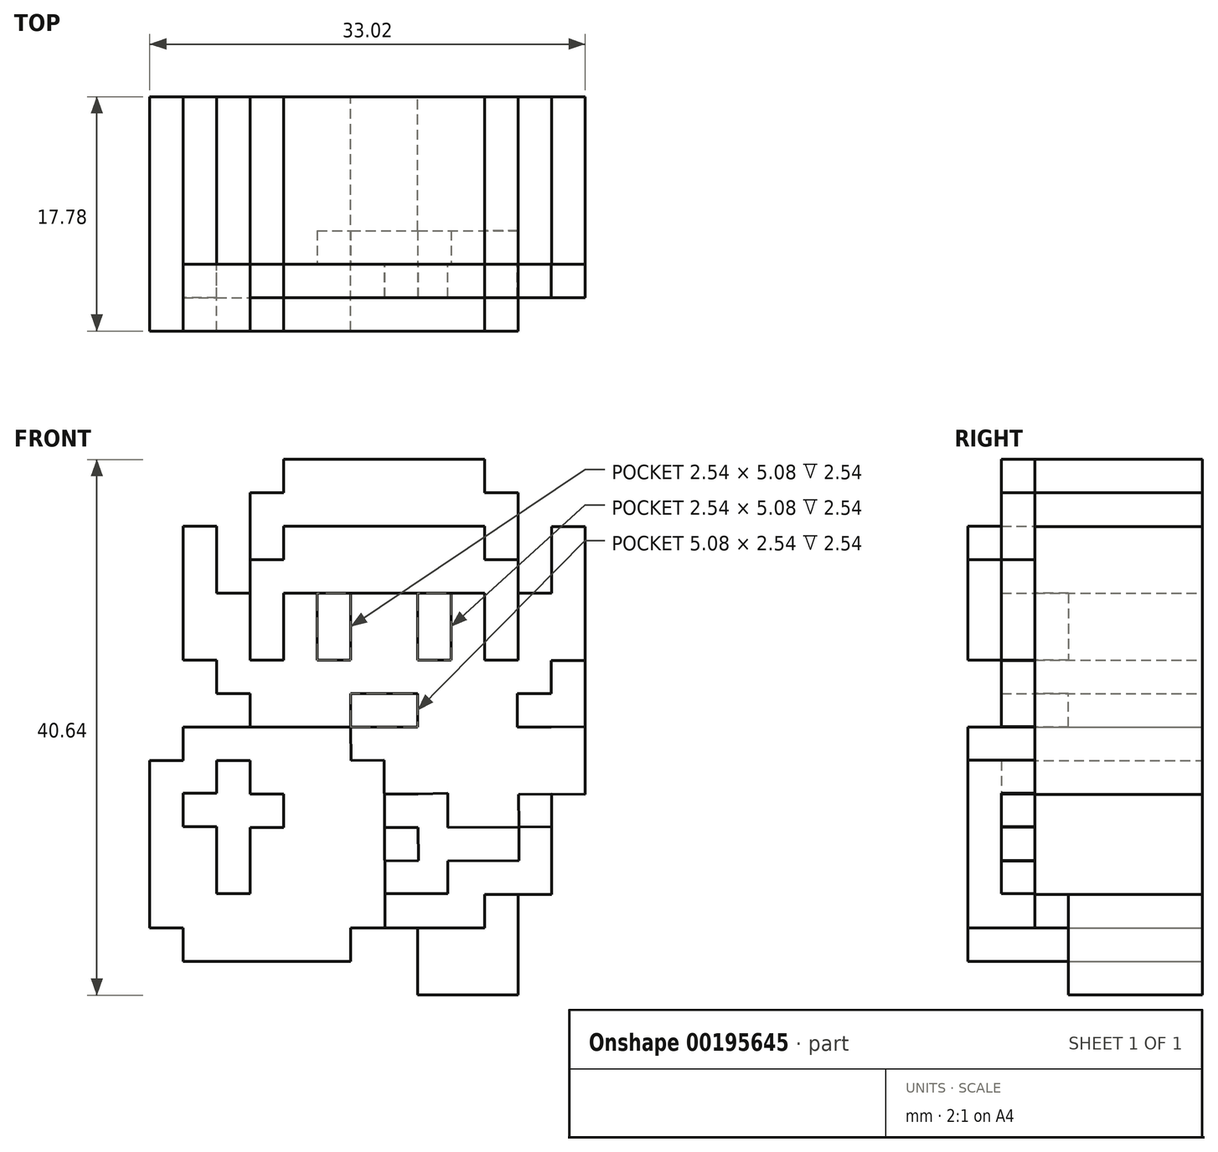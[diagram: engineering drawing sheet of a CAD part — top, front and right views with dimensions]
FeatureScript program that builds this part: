
annotation { "Feature Type Name" : "Feature", "Feature Type Description" : "" }
export const myFeature = defineFeature(function(context is Context, id is Id, definition is map)
    precondition{}
    {
        {
            var Q0;
            Q0=qCreatedBy(makeId("Front.planeOp"),FACE);
            var sketch = newSketch(context, id + "F0", { "sketchPlane" : qUnion([Q0])});
            skLineSegment(sketch, "E0", {"start": v(-12.95, 10.7) * mm, "end": v(2.29, 10.7) * mm});
            skLineSegment(sketch, "E1", {"start": v(-12.95, 10.7) * mm, "end": v(-12.95, 8.15) * mm});
            skLineSegment(sketch, "E2", {"start": v(-12.95, 8.15) * mm, "end": v(-15.5, 8.15) * mm});
            skLineSegment(sketch, "E3", {"start": v(2.29, 10.7) * mm, "end": v(2.29, 8.15) * mm});
            skLineSegment(sketch, "E4", {"start": v(2.29, 8.15) * mm, "end": v(4.83, 8.15) * mm});
            skLineSegment(sketch, "E5", {"start": v(-15.5, 8.15) * mm, "end": v(-15.5, 0.53) * mm});
            skLineSegment(sketch, "E6", {"start": v(4.83, 8.15) * mm, "end": v(4.83, 0.53) * mm});
            skLineSegment(sketch, "E7", {"start": v(-15.5, 0.53) * mm, "end": v(-18.03, 0.53) * mm});
            skLineSegment(sketch, "E8", {"start": v(-18.03, 0.53) * mm, "end": v(-18.03, 5.61) * mm});
            skLineSegment(sketch, "E9", {"start": v(-18.03, 5.61) * mm, "end": v(-20.57, 5.61) * mm});
            skLineSegment(sketch, "E10", {"start": v(-20.57, 5.61) * mm, "end": v(-20.57, -4.55) * mm});
            skLineSegment(sketch, "E11", {"start": v(-20.57, -4.55) * mm, "end": v(-18.03, -4.55) * mm});
            skLineSegment(sketch, "E12", {"start": v(-18.03, -4.55) * mm, "end": v(-18.03, -7.09) * mm});
            skLineSegment(sketch, "E13", {"start": v(-18.03, -7.09) * mm, "end": v(-15.5, -7.09) * mm});
            skLineSegment(sketch, "E14", {"start": v(-15.5, -7.09) * mm, "end": v(-15.5, -9.63) * mm});
            skLineSegment(sketch, "E15", {"start": v(4.83, 0.53) * mm, "end": v(7.37, 0.53) * mm});
            skLineSegment(sketch, "E16", {"start": v(7.37, 0.53) * mm, "end": v(7.37, 5.61) * mm});
            skLineSegment(sketch, "E17", {"start": v(7.37, 5.61) * mm, "end": v(9.9, 5.61) * mm});
            skLineSegment(sketch, "E18", {"start": v(9.9, 5.61) * mm, "end": v(9.9, -14.7) * mm});
            skLineSegment(sketch, "E19", {"start": v(-15.5, -9.63) * mm, "end": v(-20.57, -9.63) * mm});
            skLineSegment(sketch, "E20", {"start": v(-20.57, -9.63) * mm, "end": v(-20.57, -12.17) * mm});
            skLineSegment(sketch, "E21", {"start": v(-20.57, -12.17) * mm, "end": v(-23.11, -12.17) * mm});
            skLineSegment(sketch, "E22", {"start": v(-23.11, -12.17) * mm, "end": v(-23.11, -24.87) * mm});
            skLineSegment(sketch, "E23", {"start": v(-23.11, -24.87) * mm, "end": v(-20.57, -24.87) * mm});
            skLineSegment(sketch, "E24", {"start": v(-20.57, -24.87) * mm, "end": v(-20.57, -27.4) * mm});
            skLineSegment(sketch, "E25", {"start": v(-20.57, -27.4) * mm, "end": v(-7.87, -27.4) * mm});
            skLineSegment(sketch, "E26", {"start": v(-7.87, -27.4) * mm, "end": v(-7.87, -24.87) * mm});
            skLineSegment(sketch, "E27", {"start": v(-7.87, -24.87) * mm, "end": v(-2.8, -24.87) * mm});
            skLineSegment(sketch, "E28", {"start": v(-2.8, -24.87) * mm, "end": v(-2.8, -29.95) * mm});
            skLineSegment(sketch, "E29", {"start": v(-2.8, -29.95) * mm, "end": v(4.83, -29.95) * mm});
            skLineSegment(sketch, "E30", {"start": v(4.83, -29.95) * mm, "end": v(4.83, -22.33) * mm});
            skLineSegment(sketch, "E31", {"start": v(4.83, -22.33) * mm, "end": v(7.37, -22.33) * mm});
            skLineSegment(sketch, "E32", {"start": v(7.37, -22.33) * mm, "end": v(7.37, -14.7) * mm});
            skLineSegment(sketch, "E33", {"start": v(7.37, -14.7) * mm, "end": v(9.9, -14.7) * mm});
            skSolve(sketch);
        }
        {
            var Q0;
            Q0=makeQuery(id+"F0.imprint","IMPRINT",FACE,{"disambiguationData":[TD([[makeQuery(id+"F0.imprint","IMPRINT",EDGE,{"derivedFrom":sQuery(id+"F0.wireOp",EDGE,"E0")}),-1.0]])]});
            extrude(context, id + "F1", {"entities" : qUnion([Q0]), "depth" : 12.7 * mm});
        }
        {
            var Q0;
            Q0=makeQuery(id+"F1.opExtrude","CAP_FACE",FACE,{"disambiguationData":[OSD([sQuery(id+"F0.wireOp",EDGE,"E0"),sQuery(id+"F0.wireOp",EDGE,"E1"),sQuery(id+"F0.wireOp",EDGE,"E2"),sQuery(id+"F0.wireOp",EDGE,"E3"),sQuery(id+"F0.wireOp",EDGE,"E4"),sQuery(id+"F0.wireOp",EDGE,"E5"),sQuery(id+"F0.wireOp",EDGE,"E6"),sQuery(id+"F0.wireOp",EDGE,"E7"),sQuery(id+"F0.wireOp",EDGE,"E8"),sQuery(id+"F0.wireOp",EDGE,"E9"),sQuery(id+"F0.wireOp",EDGE,"E10"),sQuery(id+"F0.wireOp",EDGE,"E11"),sQuery(id+"F0.wireOp",EDGE,"E12"),sQuery(id+"F0.wireOp",EDGE,"E13"),sQuery(id+"F0.wireOp",EDGE,"E14"),sQuery(id+"F0.wireOp",EDGE,"E15"),sQuery(id+"F0.wireOp",EDGE,"E16"),sQuery(id+"F0.wireOp",EDGE,"E17"),sQuery(id+"F0.wireOp",EDGE,"E18"),sQuery(id+"F0.wireOp",EDGE,"E19"),sQuery(id+"F0.wireOp",EDGE,"E20"),sQuery(id+"F0.wireOp",EDGE,"E21"),sQuery(id+"F0.wireOp",EDGE,"E22"),sQuery(id+"F0.wireOp",EDGE,"E23"),sQuery(id+"F0.wireOp",EDGE,"E24"),sQuery(id+"F0.wireOp",EDGE,"E25"),sQuery(id+"F0.wireOp",EDGE,"E26"),sQuery(id+"F0.wireOp",EDGE,"E27"),sQuery(id+"F0.wireOp",EDGE,"E28"),sQuery(id+"F0.wireOp",EDGE,"E29"),sQuery(id+"F0.wireOp",EDGE,"E30"),sQuery(id+"F0.wireOp",EDGE,"E31"),sQuery(id+"F0.wireOp",EDGE,"E32"),sQuery(id+"F0.wireOp",EDGE,"E33")])],"isStart":false});
            var sketch = newSketch(context, id + "F2", { "sketchPlane" : qUnion([Q0])});
            skLineSegment(sketch, "E34", {"start": v(-15.5, 8.15) * mm, "end": v(-15.5, 3.07) * mm});
            skLineSegment(sketch, "E35", {"start": v(-15.5, 3.07) * mm, "end": v(-12.95, 3.07) * mm});
            skLineSegment(sketch, "E36", {"start": v(-12.95, 3.07) * mm, "end": v(-12.95, 5.61) * mm});
            skLineSegment(sketch, "E37", {"start": v(-12.95, 5.61) * mm, "end": v(2.3, 5.61) * mm});
            skLineSegment(sketch, "E38", {"start": v(2.3, 5.61) * mm, "end": v(2.3, 3.07) * mm});
            skLineSegment(sketch, "E39", {"start": v(2.3, 3.07) * mm, "end": v(4.83, 3.07) * mm});
            skLineSegment(sketch, "E40", {"start": v(-15.5, 0.53) * mm, "end": v(-15.5, -4.55) * mm});
            skLineSegment(sketch, "E41", {"start": v(-15.5, -4.55) * mm, "end": v(-12.95, -4.55) * mm});
            skLineSegment(sketch, "E42", {"start": v(-12.95, -4.55) * mm, "end": v(-12.95, 0.53) * mm});
            skLineSegment(sketch, "E43", {"start": v(-12.95, 0.53) * mm, "end": v(2.29, 0.53) * mm});
            skLineSegment(sketch, "E44", {"start": v(2.29, 0.53) * mm, "end": v(2.29, -4.55) * mm});
            skLineSegment(sketch, "E45", {"start": v(2.29, -4.55) * mm, "end": v(4.83, -4.55) * mm});
            skLineSegment(sketch, "E46", {"start": v(4.83, -4.55) * mm, "end": v(4.83, 0.53) * mm});
            skLineSegment(sketch, "E47", {"start": v(-12.95, 0.53) * mm, "end": v(-10.41, 0.53) * mm});
            skLineSegment(sketch, "E48", {"start": v(-10.41, 0.53) * mm, "end": v(-10.41, -4.55) * mm});
            skLineSegment(sketch, "E49", {"start": v(-10.41, -4.55) * mm, "end": v(-7.87, -4.55) * mm});
            skLineSegment(sketch, "E50", {"start": v(-7.87, -4.55) * mm, "end": v(-7.87, 0.53) * mm});
            skLineSegment(sketch, "E51", {"start": v(-7.87, 0.53) * mm, "end": v(-2.8, 0.53) * mm});
            skLineSegment(sketch, "E52", {"start": v(-2.8, 0.53) * mm, "end": v(-2.8, -4.55) * mm});
            skLineSegment(sketch, "E53", {"start": v(-2.8, -4.55) * mm, "end": v(-0.26, -4.55) * mm});
            skLineSegment(sketch, "E54", {"start": v(-0.26, -4.55) * mm, "end": v(-0.26, 0.53) * mm});
            skLineSegment(sketch, "E55", {"start": v(-7.87, -7.06) * mm, "end": v(-2.8, -7.06) * mm});
            skLineSegment(sketch, "E56", {"start": v(-2.8, -7.06) * mm, "end": v(-2.8, -9.6) * mm});
            skLineSegment(sketch, "E57", {"start": v(-2.8, -9.6) * mm, "end": v(-7.87, -9.6) * mm});
            skLineSegment(sketch, "E58", {"start": v(-7.87, -9.6) * mm, "end": v(-7.87, -7.06) * mm});
            skLineSegment(sketch, "E59", {"start": v(-15.5, -7.09) * mm, "end": v(-12.95, -7.09) * mm});
            skLineSegment(sketch, "E60", {"start": v(-12.95, -7.09) * mm, "end": v(-12.95, -9.63) * mm});
            skLineSegment(sketch, "E61", {"start": v(-12.95, -9.63) * mm, "end": v(-15.5, -9.63) * mm});
            skLineSegment(sketch, "E62", {"start": v(-12.95, -9.63) * mm, "end": v(-7.87, -9.6) * mm});
            skLineSegment(sketch, "E63", {"start": v(-7.87, -9.6) * mm, "end": v(-7.86, -12.14) * mm});
            skLineSegment(sketch, "E64", {"start": v(-7.86, -12.14) * mm, "end": v(-5.32, -12.12) * mm});
            skPoint(sketch, "E65.endSnap0", {"position": v(-5.33, -24.87) * mm});
            skLineSegment(sketch, "E66", {"start": v(-5.32, -12.12) * mm, "end": v(-5.27, -22.26) * mm});
            skLineSegment(sketch, "E67", {"start": v(-20.57, -12.17) * mm, "end": v(-18.03, -12.17) * mm});
            skLineSegment(sketch, "E68", {"start": v(-18.03, -12.17) * mm, "end": v(-18.03, -14.62) * mm});
            skLineSegment(sketch, "E69", {"start": v(-18.03, -12.17) * mm, "end": v(-15.49, -12.17) * mm});
            skLineSegment(sketch, "E70", {"start": v(-15.49, -12.17) * mm, "end": v(-15.49, -14.7) * mm});
            skLineSegment(sketch, "E71", {"start": v(-15.49, -14.7) * mm, "end": v(-12.95, -14.7) * mm});
            skLineSegment(sketch, "E72", {"start": v(-12.95, -14.7) * mm, "end": v(-12.95, -17.25) * mm});
            skLineSegment(sketch, "E73", {"start": v(-12.95, -17.25) * mm, "end": v(-15.49, -17.25) * mm});
            skLineSegment(sketch, "E74", {"start": v(-18.03, -14.62) * mm, "end": v(-20.57, -14.62) * mm});
            skLineSegment(sketch, "E75", {"start": v(-20.57, -14.62) * mm, "end": v(-20.57, -17.16) * mm});
            skLineSegment(sketch, "E76", {"start": v(-20.57, -17.16) * mm, "end": v(-18.03, -17.16) * mm});
            skLineSegment(sketch, "E77", {"start": v(-18.03, -17.16) * mm, "end": v(-18.03, -22.24) * mm});
            skLineSegment(sketch, "E78", {"start": v(-18.03, -22.24) * mm, "end": v(-15.49, -22.24) * mm});
            skLineSegment(sketch, "E79", {"start": v(-15.49, -22.24) * mm, "end": v(-15.49, -17.25) * mm});
            skLineSegment(sketch, "E80", {"start": v(-5.32, -12.12) * mm, "end": v(-5.3, -14.68) * mm});
            skLineSegment(sketch, "E81", {"start": v(-5.3, -14.68) * mm, "end": v(-2.77, -14.68) * mm});
            skLineSegment(sketch, "E82", {"start": v(-2.76, -17.22) * mm, "end": v(-5.3, -17.22) * mm});
            skLineSegment(sketch, "E83", {"start": v(-2.76, -17.22) * mm, "end": v(-2.74, -19.75) * mm});
            skLineSegment(sketch, "E84", {"start": v(-2.74, -19.75) * mm, "end": v(-5.3, -19.76) * mm});
            skLineSegment(sketch, "E85", {"start": v(-2.73, -22.24) * mm, "end": v(-5.27, -22.26) * mm});
            skLineSegment(sketch, "E86", {"start": v(-2.73, -22.24) * mm, "end": v(-0.52, -22.24) * mm});
            skLineSegment(sketch, "E87", {"start": v(-0.52, -22.24) * mm, "end": v(-0.52, -19.78) * mm});
            skLineSegment(sketch, "E88", {"start": v(-0.52, -14.62) * mm, "end": v(-2.77, -14.68) * mm});
            skLineSegment(sketch, "E89", {"start": v(-0.52, -17.22) * mm, "end": v(7.37, -17.17) * mm});
            skLineSegment(sketch, "E90", {"start": v(7.37, -14.7) * mm, "end": v(4.87, -14.72) * mm});
            skLineSegment(sketch, "E91", {"start": v(4.87, -14.72) * mm, "end": v(4.88, -17.17) * mm});
            skLineSegment(sketch, "E92", {"start": v(4.88, -17.17) * mm, "end": v(4.9, -19.75) * mm});
            skLineSegment(sketch, "E93", {"start": v(4.9, -19.75) * mm, "end": v(-0.52, -19.78) * mm});
            skLineSegment(sketch, "E94", {"start": v(7.37, -14.7) * mm, "end": v(7.34, -9.6) * mm});
            skLineSegment(sketch, "E95", {"start": v(7.34, -9.6) * mm, "end": v(9.9, -9.59) * mm});
            skLineSegment(sketch, "E96", {"start": v(9.9, -9.59) * mm, "end": v(9.9, -4.55) * mm});
            skLineSegment(sketch, "E97", {"start": v(9.9, -4.55) * mm, "end": v(7.34, -4.55) * mm});
            skLineSegment(sketch, "E98", {"start": v(7.34, -4.55) * mm, "end": v(7.34, -7.07) * mm});
            skPoint(sketch, "E98.endSnap0", {"position": v(9.9, -7.07) * mm});
            skLineSegment(sketch, "E99", {"start": v(7.34, -7.07) * mm, "end": v(4.76, -7.07) * mm});
            skLineSegment(sketch, "E100", {"start": v(4.76, -7.07) * mm, "end": v(4.76, -9.6) * mm});
            skLineSegment(sketch, "E101", {"start": v(4.76, -9.6) * mm, "end": v(7.34, -9.6) * mm});
            skLineSegment(sketch, "E102", {"start": v(-2.8, -24.87) * mm, "end": v(2.28, -24.87) * mm});
            skPoint(sketch, "E102.endSnap0", {"position": v(4.83, -26.14) * mm});
            skLineSegment(sketch, "E103", {"start": v(4.83, -24.87) * mm, "end": v(4.83, -22.33) * mm});
            skLineSegment(sketch, "E104", {"start": v(4.83, -22.33) * mm, "end": v(2.28, -22.33) * mm});
            skLineSegment(sketch, "E105", {"start": v(2.28, -22.33) * mm, "end": v(2.28, -24.87) * mm});
            skLineSegment(sketch, "E106", {"start": v(-5.27, -22.26) * mm, "end": v(-5.27, -25.62) * mm});
            skPoint(sketch, "E107.end.orphan", {"position": v(-7.87, -2) * mm});
            skPoint(sketch, "E107.start.orphan", {"position": v(-10.41, -2) * mm});
            skPoint(sketch, "E108.end.orphan", {"position": v(-0.26, -2) * mm});
            skPoint(sketch, "E108.start.orphan", {"position": v(-2.8, -2) * mm});
            skLineSegment(sketch, "E109.trimOffspring", {"start": v(-0.52, -17.22) * mm, "end": v(-0.52, -14.62) * mm});
            skLineSegment(sketch, "E110.0.0", {"start": v(2.29, 10.7) * mm, "end": v(-12.95, 10.7) * mm});
            skLineSegment(sketch, "E110.0.1", {"start": v(-12.95, 10.7) * mm, "end": v(-12.95, 8.15) * mm});
            skLineSegment(sketch, "E110.0.2", {"start": v(-12.95, 8.15) * mm, "end": v(-15.5, 8.15) * mm});
            skLineSegment(sketch, "E110.0.3", {"start": v(-15.5, 8.15) * mm, "end": v(-15.5, 0.53) * mm});
            skLineSegment(sketch, "E110.0.4", {"start": v(-15.5, 0.53) * mm, "end": v(-18.03, 0.53) * mm});
            skLineSegment(sketch, "E110.0.5", {"start": v(-18.03, 0.53) * mm, "end": v(-18.03, 5.61) * mm});
            skLineSegment(sketch, "E110.0.6", {"start": v(-18.03, 5.61) * mm, "end": v(-20.57, 5.61) * mm});
            skLineSegment(sketch, "E110.0.7", {"start": v(-20.57, 5.61) * mm, "end": v(-20.57, -4.55) * mm});
            skLineSegment(sketch, "E110.0.8", {"start": v(-20.57, -4.55) * mm, "end": v(-18.03, -4.55) * mm});
            skLineSegment(sketch, "E110.0.9", {"start": v(-18.03, -4.55) * mm, "end": v(-18.03, -7.09) * mm});
            skLineSegment(sketch, "E110.0.10", {"start": v(-18.03, -7.09) * mm, "end": v(-15.5, -7.09) * mm});
            skLineSegment(sketch, "E110.0.11", {"start": v(-15.5, -7.09) * mm, "end": v(-15.5, -9.63) * mm});
            skLineSegment(sketch, "E110.0.12", {"start": v(-15.5, -9.63) * mm, "end": v(-20.57, -9.63) * mm});
            skLineSegment(sketch, "E110.0.13", {"start": v(-20.57, -9.63) * mm, "end": v(-20.57, -12.17) * mm});
            skLineSegment(sketch, "E110.0.14", {"start": v(-20.57, -12.17) * mm, "end": v(-23.11, -12.17) * mm});
            skLineSegment(sketch, "E110.0.15", {"start": v(-23.11, -12.17) * mm, "end": v(-23.11, -24.87) * mm});
            skLineSegment(sketch, "E110.0.16", {"start": v(-23.11, -24.87) * mm, "end": v(-20.57, -24.87) * mm});
            skLineSegment(sketch, "E110.0.17", {"start": v(-20.57, -24.87) * mm, "end": v(-20.57, -27.4) * mm});
            skLineSegment(sketch, "E110.0.18", {"start": v(-20.57, -27.4) * mm, "end": v(-7.87, -27.4) * mm});
            skLineSegment(sketch, "E110.0.19", {"start": v(-7.87, -27.4) * mm, "end": v(-7.87, -24.87) * mm});
            skLineSegment(sketch, "E110.0.20", {"start": v(-7.87, -24.87) * mm, "end": v(-2.8, -24.87) * mm});
            skLineSegment(sketch, "E110.0.21", {"start": v(-2.8, -24.87) * mm, "end": v(-2.8, -29.95) * mm});
            skLineSegment(sketch, "E110.0.22", {"start": v(-2.8, -29.95) * mm, "end": v(4.83, -29.95) * mm});
            skLineSegment(sketch, "E110.0.23", {"start": v(4.83, -29.95) * mm, "end": v(4.83, -22.33) * mm});
            skLineSegment(sketch, "E110.0.24", {"start": v(4.83, -22.33) * mm, "end": v(7.37, -22.33) * mm});
            skLineSegment(sketch, "E110.0.25", {"start": v(7.37, -22.33) * mm, "end": v(7.37, -14.7) * mm});
            skLineSegment(sketch, "E110.0.26", {"start": v(7.37, -14.7) * mm, "end": v(9.9, -14.7) * mm});
            skLineSegment(sketch, "E110.0.27", {"start": v(9.9, -14.7) * mm, "end": v(9.9, 5.61) * mm});
            skLineSegment(sketch, "E110.0.28", {"start": v(9.9, 5.61) * mm, "end": v(7.37, 5.61) * mm});
            skLineSegment(sketch, "E110.0.29", {"start": v(7.37, 5.61) * mm, "end": v(7.37, 0.53) * mm});
            skLineSegment(sketch, "E110.0.30", {"start": v(7.37, 0.53) * mm, "end": v(4.83, 0.53) * mm});
            skLineSegment(sketch, "E110.0.31", {"start": v(4.83, 0.53) * mm, "end": v(4.83, 8.15) * mm});
            skLineSegment(sketch, "E110.0.32", {"start": v(4.83, 8.15) * mm, "end": v(2.29, 8.15) * mm});
            skLineSegment(sketch, "E110.0.33", {"start": v(2.29, 8.15) * mm, "end": v(2.29, 10.7) * mm});
            skSolve(sketch);
        }
        {
            var Q0;
            Q0=makeQuery(id+"F2.imprint","IMPRINT",FACE,{"disambiguationData":[TD([[makeQuery(id+"F2.imprint","IMPRINT",EDGE,{"derivedFrom":sQuery(id+"F2.wireOp",EDGE,"E61")}),1.0]])]});
            var Q1;
            {var subQ1=sQuery(id+"F2.wireOp",EDGE,"E35");Q1=makeQuery(id+"F2.imprint","IMPRINT",FACE,{"disambiguationData":[TD([[makeQuery(id+"F2.imprint","IMPRINT",EDGE,{"derivedFrom":subQ1}),-1.0]])]});}
            var Q2;
            Q2=makeQuery(id+"F2.imprint","IMPRINT",FACE,{"disambiguationData":[TD([[makeQuery(id+"F2.imprint","IMPRINT",EDGE,{"derivedFrom":sQuery(id+"F2.wireOp",EDGE,"bvazWGpX-JiwJ-38wZ-IpHl-hfmCeXnEQCwH")}),-1.0]])]});
            var Q3;
            Q3=makeQuery(id+"F2.imprint","IMPRINT",FACE,{"disambiguationData":[TD([[makeQuery(id+"F2.imprint","IMPRINT",EDGE,{"derivedFrom":sQuery(id+"F2.wireOp",EDGE,"E64")}),-1.0]])]});
            extrude(context, id + "F3", {"entities" : qUnion([Q0, Q1, Q2, Q3]), "operationType" : NewBodyOperationType.ADD, "depth" : 5.08 * mm});
        }
        {
            var Q0;
            {var subQ1=sQuery(id+"F2.wireOp",EDGE,"E35");Q0=makeQuery(id+"F2.imprint","IMPRINT",FACE,{"disambiguationData":[TD([[makeQuery(id+"F2.imprint","IMPRINT",EDGE,{"derivedFrom":subQ1}),-1.0]])]});}
            var Q1;
            {var subQ2=sQuery(id+"F2.wireOp",EDGE,"E81");Q1=makeQuery(id+"F2.imprint","IMPRINT",FACE,{"disambiguationData":[TD([[makeQuery(id+"F2.imprint","IMPRINT",EDGE,{"derivedFrom":subQ2}),-1.0]])]});}
            var Q2;
            {var subQ3=sQuery(id+"F2.wireOp",EDGE,"E93");Q2=makeQuery(id+"F2.imprint","IMPRINT",FACE,{"disambiguationData":[TD([[makeQuery(id+"F2.imprint","IMPRINT",EDGE,{"derivedFrom":subQ3}),-1.0]])]});}
            var Q3;
            {var subQ4=sQuery(id+"F2.wireOp",EDGE,"E90");Q3=makeQuery(id+"F2.imprint","IMPRINT",FACE,{"disambiguationData":[TD([[makeQuery(id+"F2.imprint","IMPRINT",EDGE,{"derivedFrom":subQ4}),1.0]])]});}
            var Q4;
            Q4=makeQuery(id+"F2.imprint","IMPRINT",FACE,{"disambiguationData":[TD([[makeQuery(id+"F2.imprint","IMPRINT",EDGE,{"derivedFrom":sQuery(id+"F2.wireOp",EDGE,"E95")}),1.0]])]});
            var Q5;
            Q5=makeQuery(id+"F2.imprint","IMPRINT",FACE,{"disambiguationData":[TD([[makeQuery(id+"F2.imprint","IMPRINT",EDGE,{"derivedFrom":sQuery(id+"F2.wireOp",EDGE,"E34")}),1.0]])]});
            var Q6;
            Q6=makeQuery(id+"F2.imprint","IMPRINT",FACE,{"disambiguationData":[TD([[makeQuery(id+"F2.imprint","IMPRINT",EDGE,{"derivedFrom":sQuery(id+"F2.wireOp",EDGE,"E68")}),1.0]])]});
            extrude(context, id + "F4", {"entities" : qUnion([Q0, Q1, Q2, Q3, Q4, Q5, Q6]), "depth" : 2.54 * mm});
        }
        {
            var Q0;
            {var subQ0=sQuery(id+"F2.wireOp",EDGE,"E48");Q0=makeQuery(id+"F2.imprint","IMPRINT",FACE,{"disambiguationData":[TD([[makeQuery(id+"F2.imprint","IMPRINT",EDGE,{"derivedFrom":subQ0}),1.0]])]});}
            var Q1;
            {var subQ0=sQuery(id+"F2.wireOp",EDGE,"E52");Q1=makeQuery(id+"F2.imprint","IMPRINT",FACE,{"disambiguationData":[TD([[makeQuery(id+"F2.imprint","IMPRINT",EDGE,{"derivedFrom":subQ0}),1.0]])]});}
            var Q2;
            Q2=makeQuery(id+"F2.imprint","IMPRINT",FACE,{"disambiguationData":[TD([[makeQuery(id+"F2.imprint","IMPRINT",EDGE,{"derivedFrom":sQuery(id+"F2.wireOp",EDGE,"E55")}),-1.0]])]});
            var Q3;
            Q3=makeQuery(id+"F2.imprint","IMPRINT",FACE,{"disambiguationData":[TD([[makeQuery(id+"F2.imprint","IMPRINT",EDGE,{"derivedFrom":sQuery(id+"F2.wireOp",EDGE,"E102")}),-1.0]])]});
            extrude(context, id + "F5", {"entities" : qUnion([Q0, Q1, Q2, Q3]), "operationType" : NewBodyOperationType.REMOVE, "oppositeDirection" : true, "depth" : 2.54 * mm});
        }
    });
